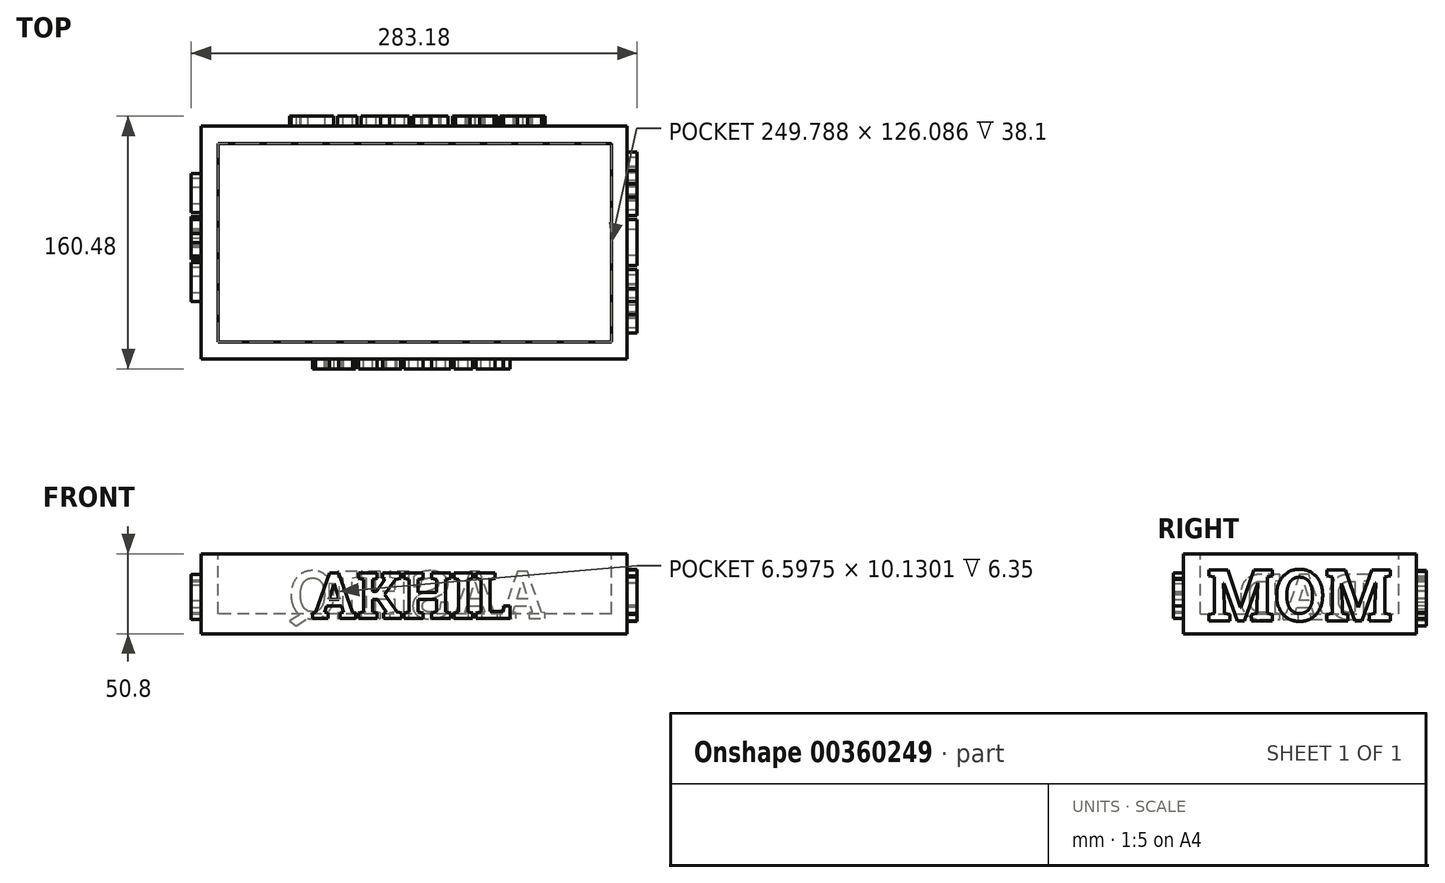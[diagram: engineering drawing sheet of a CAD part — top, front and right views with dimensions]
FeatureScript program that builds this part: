
annotation { "Feature Type Name" : "Feature", "Feature Type Description" : "" }
export const myFeature = defineFeature(function(context is Context, id is Id, definition is map)
    precondition{}
    {
        {
            var Q0;
            Q0=qCreatedBy(makeId("Top.planeOp"),FACE);
            var sketch = newSketch(context, id + "F0", { "sketchPlane" : qUnion([Q0])});
            skLineSegment(sketch, "E0.bottom", {"start": v(135.24, -73.89) * mm, "end": v(-135.24, -73.89) * mm});
            skLineSegment(sketch, "E0.top", {"start": v(135.24, 73.89) * mm, "end": v(-135.24, 73.89) * mm});
            skLineSegment(sketch, "E0.left", {"start": v(135.24, -73.89) * mm, "end": v(135.24, 73.89) * mm});
            skLineSegment(sketch, "E0.right", {"start": v(-135.24, -73.89) * mm, "end": v(-135.24, 73.89) * mm});
            skPoint(sketch, "E0.middle", {"position": v(0, 0) * mm});
            skSolve(sketch);
        }
        {
            var Q0;
            Q0 = qSketchRegion(id + "F0", true);
            extrude(context, id + "F1", {"entities" : qUnion([Q0]), "depth" : 50.8 * mm});
        }
        {
            var Q0;
            Q0=makeQuery(id+"F1.opExtrude","CAP_FACE",FACE,{"disambiguationData":[OSD([sQuery(id+"F0.wireOp",EDGE,"E0.bottom"),sQuery(id+"F0.wireOp",EDGE,"E0.top"),sQuery(id+"F0.wireOp",EDGE,"E0.left"),sQuery(id+"F0.wireOp",EDGE,"E0.right")])],"isStart":false});
            var sketch = newSketch(context, id + "F2", { "sketchPlane" : qUnion([Q0])});
            skLineSegment(sketch, "E1.bottom", {"start": v(125.2, -63.2) * mm, "end": v(-124.6, -63.2) * mm});
            skLineSegment(sketch, "E1.top", {"start": v(125.2, 62.89) * mm, "end": v(-124.6, 62.89) * mm});
            skLineSegment(sketch, "E1.left", {"start": v(125.2, -63.2) * mm, "end": v(125.2, 62.89) * mm});
            skLineSegment(sketch, "E1.right", {"start": v(-124.6, -63.2) * mm, "end": v(-124.6, 62.89) * mm});
            skPoint(sketch, "E1.middle", {"position": v(0.3, -0.15) * mm});
            skSolve(sketch);
        }
        {
            var Q0;
            Q0 = qSketchRegion(id + "F2", true);
            var Q1;
            Q1 = qSketchRegion(id + "F0", true);
            extrude(context, id + "F3", {"entities" : qUnion([Q0, Q1]), "operationType" : NewBodyOperationType.REMOVE, "oppositeDirection" : true, "depth" : 38.1 * mm});
        }
        {
            var Q0;
            Q0=makeQuery(id+"F1.opExtrude","SWEPT_FACE",FACE,{"disambiguationData":[OSD([sQuery(id+"F0.wireOp",EDGE,"E0.top")])]});
            var sketch = newSketch(context, id + "F4", { "sketchPlane" : qUnion([Q0])});
            skText(sketch, "E2", { "text": "AASHIQ", "fontName": "RobotoSlab-Bold.ttf"});
            const initialGuessF4  = {"E2": [-0.08391, 0.00975, 1, 0, 0.03032]};
            skSetInitialGuess(sketch, initialGuessF4);
            skSolve(sketch);
        }
        {
            var Q0;
            Q0=makeQuery(id+"F1.opExtrude","SWEPT_FACE",FACE,{"disambiguationData":[OSD([sQuery(id+"F0.wireOp",EDGE,"E0.bottom")])]});
            var sketch = newSketch(context, id + "F5", { "sketchPlane" : qUnion([Q0])});
            skText(sketch, "E3", { "text": "AKHIL", "fontName": "RobotoSlab-Bold.ttf"});
            const initialGuessF5  = {"E3": [-0.06543, 0.00977, 1, 0, 0.02912]};
            skSetInitialGuess(sketch, initialGuessF5);
            skSolve(sketch);
        }
        {
            var Q0;
            Q0 = qSketchRegion(id + "F5", true);
            extrude(context, id + "F6", {"entities" : qUnion([Q0]), "operationType" : NewBodyOperationType.ADD, "depth" : 6.35 * mm});
        }
        {
            var Q0;
            Q0 = qSketchRegion(id + "F4", true);
            extrude(context, id + "F7", {"entities" : qUnion([Q0]), "operationType" : NewBodyOperationType.ADD, "depth" : 6.35 * mm});
        }
        {
            var Q0;
            Q0=makeQuery(id+"F1.opExtrude","SWEPT_FACE",FACE,{"disambiguationData":[OSD([sQuery(id+"F0.wireOp",EDGE,"E0.right")])]});
            var sketch = newSketch(context, id + "F8", { "sketchPlane" : qUnion([Q0])});
            skText(sketch, "E4", { "text": "DAD", "fontName": "RobotoSlab-Bold.ttf"});
            const initialGuessF8  = {"E4": [-0.04489, 0.00918, 1, 0, 0.02886]};
            skSetInitialGuess(sketch, initialGuessF8);
            skSolve(sketch);
        }
        {
            var Q0;
            Q0 = qSketchRegion(id + "F8", true);
            extrude(context, id + "F9", {"entities" : qUnion([Q0]), "operationType" : NewBodyOperationType.ADD, "depth" : 6.35 * mm});
        }
        {
            var Q0;
            Q0=makeQuery(id+"F1.opExtrude","SWEPT_FACE",FACE,{"disambiguationData":[OSD([sQuery(id+"F0.wireOp",EDGE,"E0.left")])]});
            var sketch = newSketch(context, id + "F10", { "sketchPlane" : qUnion([Q0])});
            skText(sketch, "E5", { "text": "MOM", "fontName": "RobotoSlab-Bold.ttf"});
            const initialGuessF10  = {"E5": [-0.05888, 0.0083, 1, 0, 0.03265]};
            skSetInitialGuess(sketch, initialGuessF10);
            skSolve(sketch);
        }
        {
            var Q0;
            Q0 = qSketchRegion(id + "F10", true);
            extrude(context, id + "F11", {"entities" : qUnion([Q0]), "operationType" : NewBodyOperationType.ADD, "depth" : 6.35 * mm});
        }
    });
